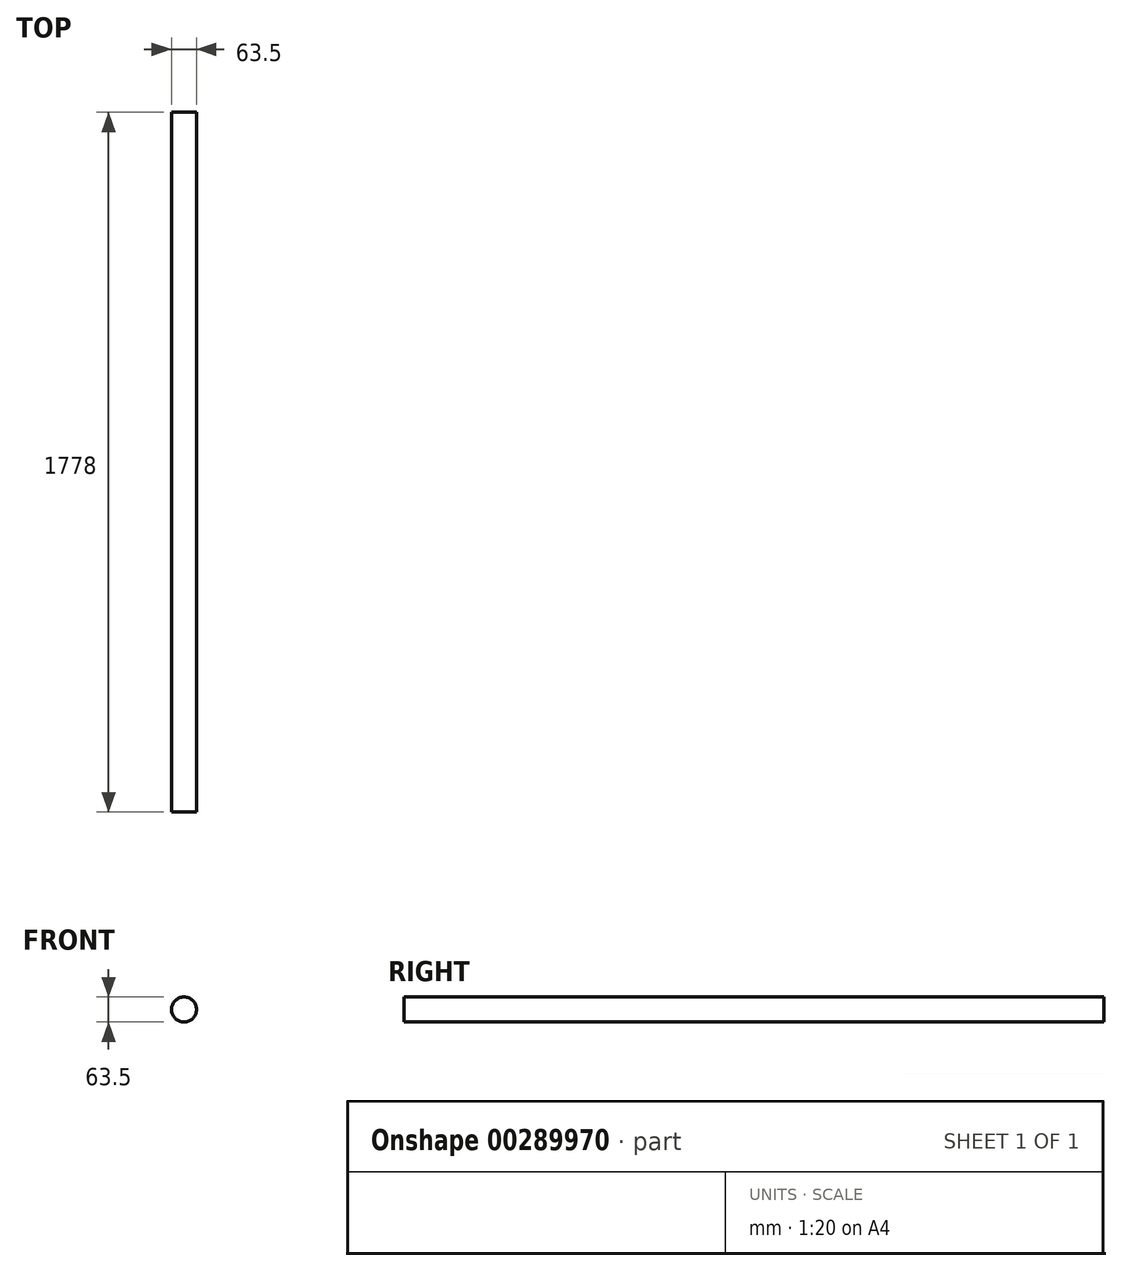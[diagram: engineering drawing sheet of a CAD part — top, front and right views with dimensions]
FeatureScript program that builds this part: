
annotation { "Feature Type Name" : "Feature", "Feature Type Description" : "" }
export const myFeature = defineFeature(function(context is Context, id is Id, definition is map)
    precondition{}
    {
        {
            var Q0;
            Q0=qCreatedBy(makeId("Front.planeOp"),FACE);
            var sketch = newSketch(context, id + "F0", { "sketchPlane" : qUnion([Q0])});
            skCircle(sketch, "E0", {"center": v(0, 0) * mm, "radius": 31.75 * mm});
            skSolve(sketch);
        }
        {
            var Q0;
            Q0 = qSketchRegion(id + "F0", true);
            extrude(context, id + "F1", {"entities" : qUnion([Q0]), "depth" : 1778 * mm});
        }
    });
